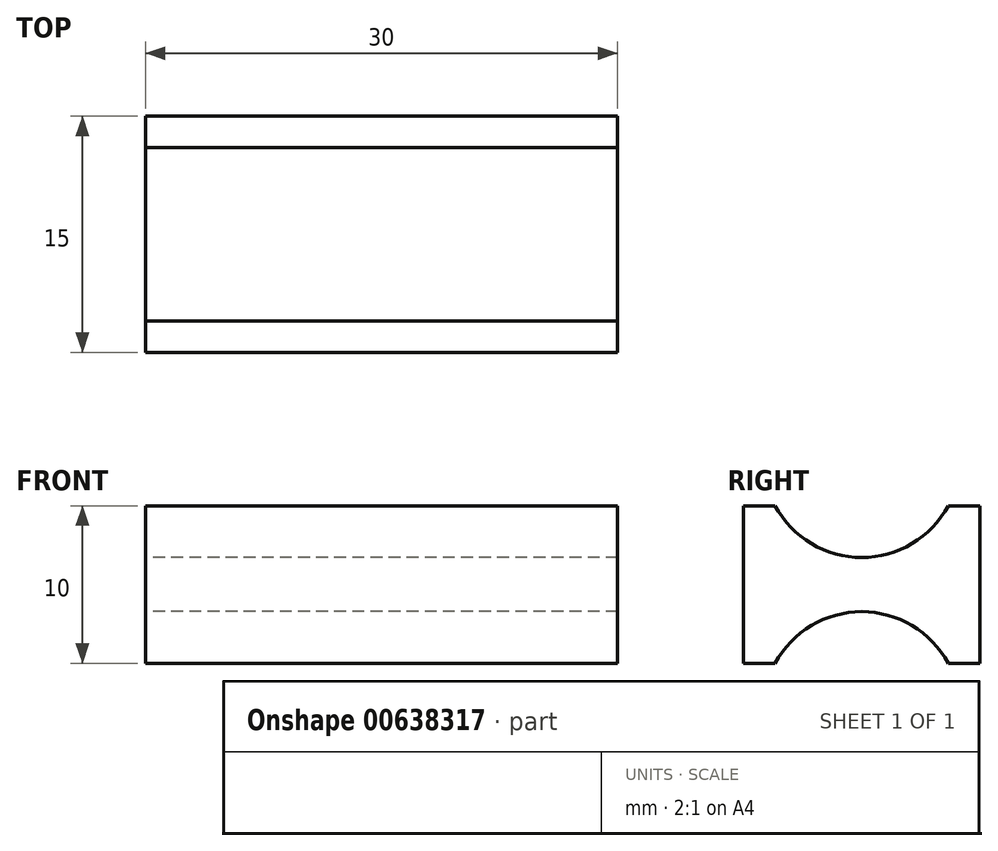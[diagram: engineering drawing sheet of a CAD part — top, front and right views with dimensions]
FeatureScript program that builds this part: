
annotation { "Feature Type Name" : "Feature", "Feature Type Description" : "" }
export const myFeature = defineFeature(function(context is Context, id is Id, definition is map)
    precondition{}
    {
        {
            var Q0;
            Q0=qCreatedBy(makeId("Top.planeOp"),FACE);
            var sketch = newSketch(context, id + "F0", { "sketchPlane" : qUnion([Q0])});
            skLineSegment(sketch, "E0.bottom", {"start": v(0, 0) * mm, "end": v(-30, 0) * mm});
            skLineSegment(sketch, "E0.top", {"start": v(0, -15) * mm, "end": v(-30, -15) * mm});
            skLineSegment(sketch, "E0.left", {"start": v(0, 0) * mm, "end": v(0, -15) * mm});
            skLineSegment(sketch, "E0.right", {"start": v(-30, 0) * mm, "end": v(-30, -15) * mm});
            skSolve(sketch);
        }
        {
            var Q0;
            Q0 = qSketchRegion(id + "F0", true);
            extrude(context, id + "F1", {"entities" : qUnion([Q0]), "depth" : 10 * mm, "offsetDistance" : 25 * mm});
        }
        {
            var Q0;
            Q0=makeQuery(id+"F1.opExtrude","SWEPT_FACE",FACE,{"disambiguationData":[OSD([sQuery(id+"F0.wireOp",EDGE,"E0.right")])]});
            var sketch = newSketch(context, id + "F2", { "sketchPlane" : qUnion([Q0])});
            skCircle(sketch, "E1", {"center": v(7.5, 12.97) * mm, "radius": 6.25 * mm});
            skPoint(sketch, "E2", {"position": v(7.5, 10) * mm});
            skLineSegment(sketch, "E3", {"start": v(0, 5) * mm, "end": v(15, 5) * mm, "construction": true});
            skCircle(sketch, "E4.MirrorC", {"center": v(7.5, -2.97) * mm, "radius": 6.25 * mm});
            skSolve(sketch);
        }
        {
            var Q0;
            Q0 = qSketchRegion(id + "F2", true);
            extrude(context, id + "F3", {"entities" : qUnion([Q0]), "operationType" : NewBodyOperationType.REMOVE, "oppositeDirection" : true, "depth" : 30 * mm, "offsetDistance" : 25 * mm});
        }
    });
